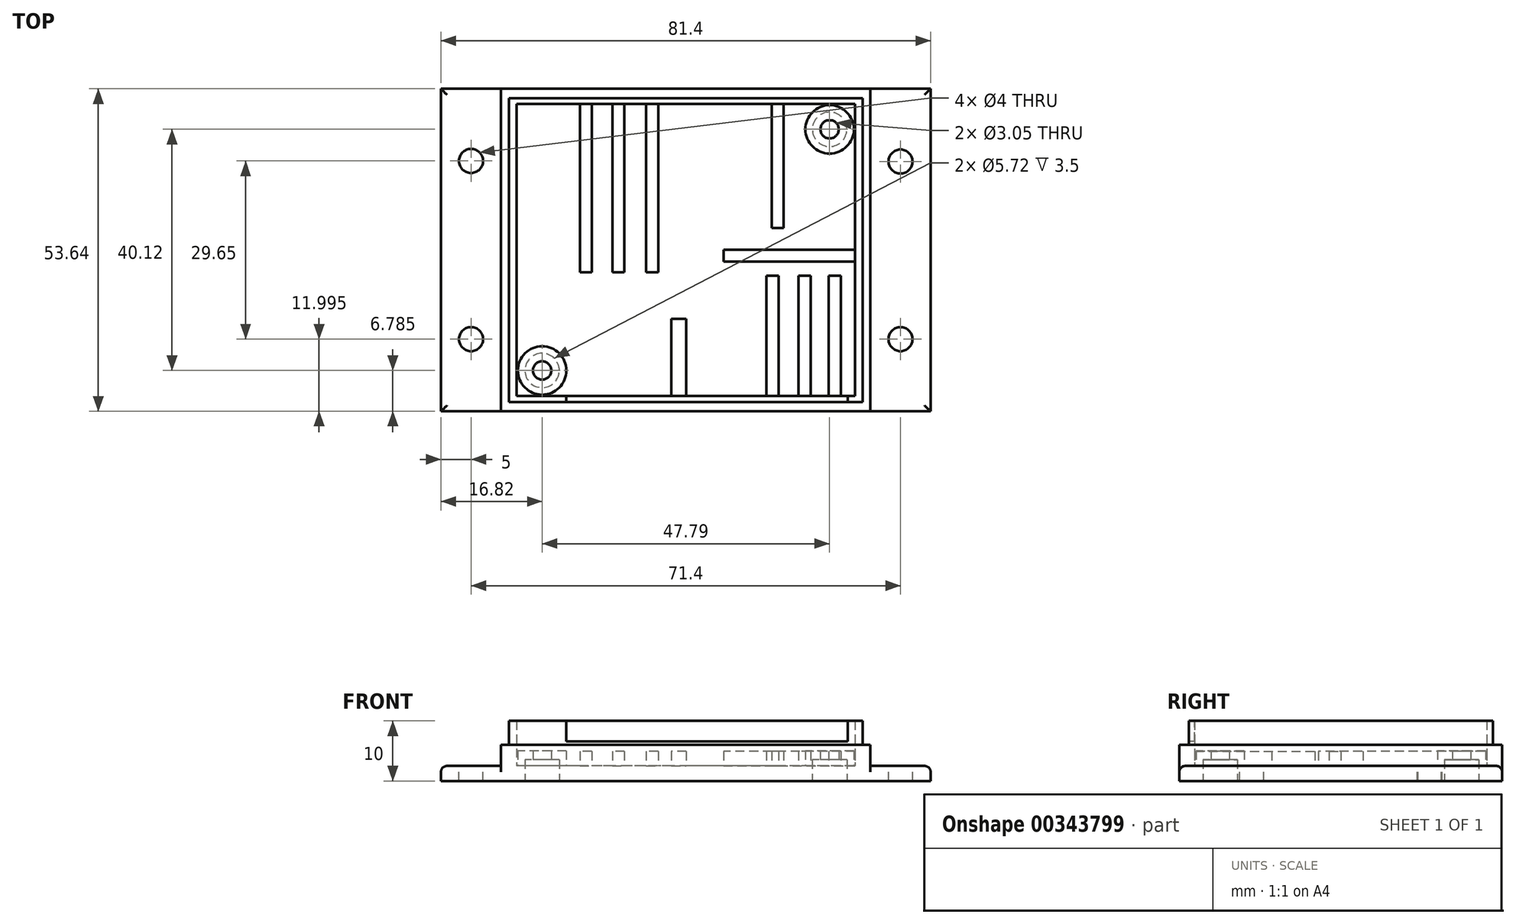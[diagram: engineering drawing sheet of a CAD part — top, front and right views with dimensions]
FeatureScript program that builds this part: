
annotation { "Feature Type Name" : "Feature", "Feature Type Description" : "" }
export const myFeature = defineFeature(function(context is Context, id is Id, definition is map)
    precondition{}
    {
        {
            var Q0;
            Q0=qCreatedBy(makeId("Top.planeOp"),FACE);
            var sketch = newSketch(context, id + "F0", { "sketchPlane" : qUnion([Q0])});
            skLineSegment(sketch, "E0.bottom", {"start": v(26.9, -23.02) * mm, "end": v(-26.9, -23.03) * mm, "construction": true});
            skLineSegment(sketch, "E0.top", {"start": v(26.9, 23.03) * mm, "end": v(-26.9, 23.02) * mm, "construction": true});
            skLineSegment(sketch, "E0.left", {"start": v(26.9, -23.02) * mm, "end": v(26.9, 23.02) * mm, "construction": true});
            skLineSegment(sketch, "E0.right", {"start": v(-26.9, -23.03) * mm, "end": v(-26.9, 23.02) * mm, "construction": true});
            skPoint(sketch, "E0.middle", {"position": v(0, 0) * mm});
            skCircle(sketch, "E1", {"center": v(-23.88, -20.04) * mm, "radius": 1.52 * mm, "construction": true});
            skCircle(sketch, "E2", {"center": v(23.9, 20.09) * mm, "radius": 1.52 * mm, "construction": true});
            skLineSegment(sketch, "E3.0", {"start": v(-28.15, -24.27) * mm, "end": v(-28.15, 24.27) * mm});
            skLineSegment(sketch, "E3.1", {"start": v(28.15, -24.27) * mm, "end": v(-28.15, -24.27) * mm});
            skLineSegment(sketch, "E3.2", {"start": v(28.15, -24.27) * mm, "end": v(28.15, 24.27) * mm});
            skLineSegment(sketch, "E3.3", {"start": v(28.15, 24.27) * mm, "end": v(-28.15, 24.27) * mm});
            skLineSegment(sketch, "E4.0", {"start": v(30.7, 26.82) * mm, "end": v(-30.7, 26.82) * mm});
            skLineSegment(sketch, "E4.1", {"start": v(30.7, -26.82) * mm, "end": v(30.7, 26.82) * mm});
            skLineSegment(sketch, "E4.2", {"start": v(30.7, -26.82) * mm, "end": v(-30.7, -26.82) * mm});
            skLineSegment(sketch, "E4.3", {"start": v(-30.7, -26.82) * mm, "end": v(-30.7, 26.82) * mm});
            skCircle(sketch, "E5", {"center": v(-23.88, -20.04) * mm, "radius": 1.52 * mm});
            skCircle(sketch, "E6", {"center": v(23.9, 20.09) * mm, "radius": 1.52 * mm});
            skCircle(sketch, "E7", {"center": v(-23.88, -20.04) * mm, "radius": 4.03 * mm});
            skCircle(sketch, "E8", {"center": v(23.9, 20.09) * mm, "radius": 4.03 * mm});
            skLineSegment(sketch, "E9.bottom", {"start": v(29.4, -25.27) * mm, "end": v(-29.4, -25.27) * mm});
            skLineSegment(sketch, "E9.top", {"start": v(29.4, 25.27) * mm, "end": v(-29.4, 25.27) * mm});
            skLineSegment(sketch, "E9.left", {"start": v(29.4, -25.27) * mm, "end": v(29.4, 25.27) * mm});
            skLineSegment(sketch, "E9.right", {"start": v(-29.4, -25.27) * mm, "end": v(-29.4, 25.27) * mm});
            skCircle(sketch, "E10", {"center": v(23.9, 20.09) * mm, "radius": 2.86 * mm});
            skCircle(sketch, "E11", {"center": v(-23.88, -20.04) * mm, "radius": 2.86 * mm});
            skLineSegment(sketch, "E12", {"start": v(26.9, -23.02) * mm, "end": v(26.9, -24.27) * mm, "construction": true});
            skCircle(sketch, "E13", {"center": v(-24.03, 20.25) * mm, "radius": 0.65 * mm, "construction": true});
            skCircle(sketch, "E14", {"center": v(-24.03, 1.2) * mm, "radius": 0.65 * mm, "construction": true});
            skCircle(sketch, "E15", {"center": v(8.99, 20.26) * mm, "radius": 0.65 * mm, "construction": true});
            skCircle(sketch, "E16", {"center": v(8.99, 7.56) * mm, "radius": 0.65 * mm, "construction": true});
            skCircle(sketch, "E17", {"center": v(-21, 20.28) * mm, "radius": 0.55 * mm, "construction": true});
            skCircle(sketch, "E18", {"center": v(-21, 12.66) * mm, "radius": 0.55 * mm, "construction": true});
            skCircle(sketch, "E19", {"center": v(-21, 7.58) * mm, "radius": 0.55 * mm, "construction": true});
            skCircle(sketch, "E20", {"center": v(-0.67, 4.12) * mm, "radius": 0.55 * mm, "construction": true});
            skCircle(sketch, "E21", {"center": v(-0.67, 10.12) * mm, "radius": 0.55 * mm, "construction": true});
            skCircle(sketch, "E22", {"center": v(-0.67, 20.28) * mm, "radius": 0.55 * mm, "construction": true});
            skCircle(sketch, "E23", {"center": v(24.2, 15.18) * mm, "radius": 0.5 * mm, "construction": true});
            skCircle(sketch, "E24", {"center": v(24.2, 12.64) * mm, "radius": 0.5 * mm, "construction": true});
            skCircle(sketch, "E25", {"center": v(24.2, 10.1) * mm, "radius": 0.5 * mm, "construction": true});
            skCircle(sketch, "E26", {"center": v(24.2, 7.56) * mm, "radius": 0.5 * mm, "construction": true});
            skCircle(sketch, "E27", {"center": v(24.2, 5.02) * mm, "radius": 0.5 * mm, "construction": true});
            skCircle(sketch, "E28", {"center": v(24.2, 2.48) * mm, "radius": 0.5 * mm, "construction": true});
            skCircle(sketch, "E29", {"center": v(-17.29, -18.54) * mm, "radius": 0.6 * mm, "construction": true});
            skCircle(sketch, "E30", {"center": v(-12.29, -18.54) * mm, "radius": 0.6 * mm, "construction": true});
            skCircle(sketch, "E31", {"center": v(-7.29, -18.54) * mm, "radius": 0.6 * mm, "construction": true});
            skCircle(sketch, "E32", {"center": v(4.95, -18.54) * mm, "radius": 0.6 * mm, "construction": true});
            skCircle(sketch, "E33", {"center": v(9.95, -18.54) * mm, "radius": 0.6 * mm, "construction": true});
            skCircle(sketch, "E34", {"center": v(-23.34, -6.12) * mm, "radius": 0.4 * mm, "construction": true});
            skCircle(sketch, "E35", {"center": v(-23.34, -11.2) * mm, "radius": 0.4 * mm, "construction": true});
            skCircle(sketch, "E36", {"center": v(-18.32, -8.1) * mm, "radius": 0.7 * mm, "construction": true});
            skCircle(sketch, "E37", {"center": v(0.11, -8.1) * mm, "radius": 0.7 * mm, "construction": true});
            skSolve(sketch);
        }
        {
            var Q0;
            Q0=makeQuery(id+"F0.imprint","IMPRINT",FACE,{"disambiguationData":[TD([[makeQuery(id+"F0.imprint","IMPRINT",EDGE,{"derivedFrom":sQuery(id+"F0.wireOp",EDGE,"E3.0")}),-1.0]])]});
            extrude(context, id + "F1", {"entities" : qUnion([Q0]), "depth" : 2.5 * mm});
        }
        {
            var Q0;
            Q0=makeQuery(id+"F0.imprint","IMPRINT",FACE,{"disambiguationData":[TD([[makeQuery(id+"F0.imprint","IMPRINT",EDGE,{"derivedFrom":sQuery(id+"F0.wireOp",EDGE,"E7")}),1.0]])]});
            var Q1;
            Q1=makeQuery(id+"F0.imprint","IMPRINT",FACE,{"disambiguationData":[TD([[makeQuery(id+"F0.imprint","IMPRINT",EDGE,{"derivedFrom":sQuery(id+"F0.wireOp",EDGE,"E5")}),-1.0]])]});
            var Q2;
            Q2=makeQuery(id+"F0.imprint","IMPRINT",FACE,{"disambiguationData":[TD([[makeQuery(id+"F0.imprint","IMPRINT",EDGE,{"derivedFrom":sQuery(id+"F0.wireOp",EDGE,"E8")}),1.0]])]});
            var Q3;
            Q3=makeQuery(id+"F0.imprint","IMPRINT",FACE,{"disambiguationData":[TD([[makeQuery(id+"F0.imprint","IMPRINT",EDGE,{"derivedFrom":sQuery(id+"F0.wireOp",EDGE,"E6")}),-1.0]])]});
            extrude(context, id + "F2", {"entities" : qUnion([Q0, Q1, Q2, Q3]), "operationType" : NewBodyOperationType.ADD, "depth" : 5 * mm});
        }
        {
            var Q0;
            Q0=makeQuery(id+"F0.imprint","IMPRINT",FACE,{"disambiguationData":[TD([[makeQuery(id+"F0.imprint","IMPRINT",EDGE,{"derivedFrom":sQuery(id+"F0.wireOp",EDGE,"E3.0")}),1.0]])]});
            extrude(context, id + "F3", {"entities" : qUnion([Q0]), "operationType" : NewBodyOperationType.ADD, "depth" : 10 * mm});
        }
        {
            var Q0;
            Q0=makeQuery(id+"F0.imprint","IMPRINT",FACE,{"disambiguationData":[TD([[makeQuery(id+"F0.imprint","IMPRINT",EDGE,{"derivedFrom":sQuery(id+"F0.wireOp",EDGE,"E4.0")}),1.0]])]});
            extrude(context, id + "F4", {"entities" : qUnion([Q0]), "operationType" : NewBodyOperationType.ADD, "depth" : 6 * mm});
        }
        {
            var Q0;
            Q0=makeQuery(id+"F0.imprint","IMPRINT",FACE,{"disambiguationData":[TD([[makeQuery(id+"F0.imprint","IMPRINT",EDGE,{"derivedFrom":sQuery(id+"F0.wireOp",EDGE,"E5")}),-1.0]])]});
            var Q1;
            Q1=makeQuery(id+"F0.imprint","IMPRINT",FACE,{"disambiguationData":[TD([[makeQuery(id+"F0.imprint","IMPRINT",EDGE,{"derivedFrom":sQuery(id+"F0.wireOp",EDGE,"E6")}),-1.0]])]});
            extrude(context, id + "F5", {"entities" : qUnion([Q0, Q1]), "operationType" : NewBodyOperationType.REMOVE, "depth" : 3.5 * mm});
        }
        {
            var Q0;
            Q0=makeQuery(id+"F4.opExtrude","SWEPT_FACE",FACE,{"disambiguationData":[OSD([sQuery(id+"F0.wireOp",EDGE,"E4.3")])]});
            var sketch = newSketch(context, id + "F6", { "sketchPlane" : qUnion([Q0])});
            skLineSegment(sketch, "E38", {"start": v(-26.82, 2.5) * mm, "end": v(26.82, 2.5) * mm});
            skSolve(sketch);
        }
        {
            var Q0;
            Q0=makeQuery(id+"F4.opExtrude","SWEPT_FACE",FACE,{"disambiguationData":[OSD([sQuery(id+"F0.wireOp",EDGE,"E4.1")])]});
            var sketch = newSketch(context, id + "F7", { "sketchPlane" : qUnion([Q0])});
            skLineSegment(sketch, "E39", {"start": v(-26.82, 2.5) * mm, "end": v(26.82, 2.5) * mm});
            skSolve(sketch);
        }
        {
            var Q0;
            {var subQ0=sQuery(id+"F6.wireOp",EDGE,"E38");Q0=makeQuery(id+"F6.imprint","IMPRINT",FACE,{"disambiguationData":[TD([[makeQuery(id+"F6.imprint","IMPRINT",EDGE,{"derivedFrom":subQ0}),-1.0]])]});}
            extrude(context, id + "F8", {"entities" : qUnion([Q0]), "operationType" : NewBodyOperationType.ADD, "depth" : 10 * mm});
        }
        {
            var Q0;
            {var subQ0=sQuery(id+"F7.wireOp",EDGE,"E39");Q0=makeQuery(id+"F7.imprint","IMPRINT",FACE,{"disambiguationData":[TD([[makeQuery(id+"F7.imprint","IMPRINT",EDGE,{"derivedFrom":subQ0}),-1.0]])]});}
            extrude(context, id + "F9", {"entities" : qUnion([Q0]), "operationType" : NewBodyOperationType.ADD, "depth" : 10 * mm});
        }
        {
            var Q0;
            Q0=makeQuery(id+"F8.opExtrude","SWEPT_FACE",FACE,{"disambiguationData":[OSD([sQuery(id+"F6.wireOp",EDGE,"E38")])]});
            var sketch = newSketch(context, id + "F10", { "sketchPlane" : qUnion([Q0])});
            skCircle(sketch, "E40", {"center": v(-35.7, 14.82) * mm, "radius": 2 * mm});
            skCircle(sketch, "E41", {"center": v(-35.7, -14.82) * mm, "radius": 2 * mm});
            skSolve(sketch);
        }
        {
            var Q0;
            Q0=makeQuery(id+"F9.opExtrude","SWEPT_FACE",FACE,{"disambiguationData":[OSD([sQuery(id+"F7.wireOp",EDGE,"E39")])]});
            var sketch = newSketch(context, id + "F11", { "sketchPlane" : qUnion([Q0])});
            skCircle(sketch, "E42", {"center": v(35.7, -14.82) * mm, "radius": 2 * mm});
            skCircle(sketch, "E43", {"center": v(35.7, 14.73) * mm, "radius": 2 * mm});
            skSolve(sketch);
        }
        {
            var Q0;
            Q0=makeQuery(id+"F10.imprint","IMPRINT",FACE,{"disambiguationData":[TD([[makeQuery(id+"F10.imprint","IMPRINT",EDGE,{"derivedFrom":sQuery(id+"F10.wireOp",EDGE,"E40")}),1.0]])]});
            var Q1;
            Q1=makeQuery(id+"F10.imprint","IMPRINT",FACE,{"disambiguationData":[TD([[makeQuery(id+"F10.imprint","IMPRINT",EDGE,{"derivedFrom":sQuery(id+"F10.wireOp",EDGE,"E41")}),1.0]])]});
            var Q2;
            Q2=makeQuery(id+"F11.imprint","IMPRINT",FACE,{"disambiguationData":[TD([[makeQuery(id+"F11.imprint","IMPRINT",EDGE,{"derivedFrom":sQuery(id+"F11.wireOp",EDGE,"E43")}),1.0]])]});
            var Q3;
            Q3=makeQuery(id+"F11.imprint","IMPRINT",FACE,{"disambiguationData":[TD([[makeQuery(id+"F11.imprint","IMPRINT",EDGE,{"derivedFrom":sQuery(id+"F11.wireOp",EDGE,"E42")}),1.0]])]});
            extrude(context, id + "F12", {"entities" : qUnion([Q0, Q1, Q2, Q3]), "operationType" : NewBodyOperationType.REMOVE, "oppositeDirection" : true, "depth" : 2.5 * mm});
        }
        {
            var Q0;
            Q0=makeQuery(id+"F3.opExtrude","CAP_FACE",FACE,{"disambiguationData":[OSD([sQuery(id+"F0.wireOp",EDGE,"E3.0"),sQuery(id+"F0.wireOp",EDGE,"E3.1"),sQuery(id+"F0.wireOp",EDGE,"E3.2"),sQuery(id+"F0.wireOp",EDGE,"E3.3"),sQuery(id+"F0.wireOp",EDGE,"E9.bottom"),sQuery(id+"F0.wireOp",EDGE,"E9.top"),sQuery(id+"F0.wireOp",EDGE,"E9.left"),sQuery(id+"F0.wireOp",EDGE,"E9.right")])],"isStart":false});
            var sketch = newSketch(context, id + "F13", { "sketchPlane" : qUnion([Q0])});
            skLineSegment(sketch, "E44", {"start": v(26.9, -24.27) * mm, "end": v(26.9, -26.77) * mm});
            skLineSegment(sketch, "E45", {"start": v(26.9, -26.77) * mm, "end": v(-19.85, -26.77) * mm});
            skLineSegment(sketch, "E46", {"start": v(-19.85, -26.77) * mm, "end": v(-19.85, -24.27) * mm});
            skSolve(sketch);
        }
        {
            var Q0;
            {var subQ0=sQuery(id+"F13.wireOp",EDGE,"E44");var subQ1=makeQuery(id+"F3.opExtrude","CAP_EDGE",EDGE,{"disambiguationData":[OSD([sQuery(id+"F0.wireOp",EDGE,"E3.1")])],"isStart":false});var subQ2=makeQuery(id+"F13.imprint","INTERSECT",VERTEX,{"derivedFrom":[subQ1,subQ0]});Q0=makeQuery(id+"F13.imprint","IMPRINT",FACE,{"disambiguationData":[TD([[makeQuery(id+"F13.imprint","IMPRINT",EDGE,{"disambiguationData":[TD([[subQ2,-1.0]])],"derivedFrom":subQ0}),-1.0]])]});}
            var Q1;
            {var subQ0=sQuery(id+"F13.wireOp",EDGE,"E45");Q1=makeQuery(id+"F13.imprint","IMPRINT",FACE,{"disambiguationData":[TD([[makeQuery(id+"F13.imprint","IMPRINT",EDGE,{"derivedFrom":subQ0}),-1.0]])]});}
            extrude(context, id + "F14", {"entities" : qUnion([Q0, Q1]), "operationType" : NewBodyOperationType.REMOVE, "oppositeDirection" : true, "depth" : 3.4 * mm});
        }
        {
            var Q0;
            Q0=makeQuery(id+"F1.opExtrude","CAP_FACE",FACE,{"disambiguationData":[OSD([sQuery(id+"F0.wireOp",EDGE,"E3.0"),sQuery(id+"F0.wireOp",EDGE,"E3.1"),sQuery(id+"F0.wireOp",EDGE,"E3.2"),sQuery(id+"F0.wireOp",EDGE,"E3.3"),sQuery(id+"F0.wireOp",EDGE,"E7"),sQuery(id+"F0.wireOp",EDGE,"E8")])],"isStart":false});
            var sketch = newSketch(context, id + "F15", { "sketchPlane" : qUnion([Q0])});
            skLineSegment(sketch, "E47", {"start": v(-12.2, 24.27) * mm, "end": v(-12.2, -3.73) * mm});
            skLineSegment(sketch, "E48", {"start": v(-12.2, -3.73) * mm, "end": v(-10.2, -3.73) * mm});
            skLineSegment(sketch, "E49", {"start": v(-10.2, -3.73) * mm, "end": v(-10.2, 24.27) * mm});
            skLineSegment(sketch, "E50", {"start": v(-6.58, 24.27) * mm, "end": v(-6.58, -3.73) * mm});
            skLineSegment(sketch, "E51", {"start": v(-6.58, -3.73) * mm, "end": v(-4.58, -3.73) * mm});
            skLineSegment(sketch, "E52", {"start": v(-4.58, -3.73) * mm, "end": v(-4.58, 24.27) * mm});
            skLineSegment(sketch, "E53", {"start": v(28.15, 0.05) * mm, "end": v(6.27, 0.05) * mm});
            skLineSegment(sketch, "E54", {"start": v(6.27, 0.05) * mm, "end": v(6.27, -1.95) * mm});
            skLineSegment(sketch, "E55", {"start": v(6.27, -1.95) * mm, "end": v(28.15, -1.95) * mm});
            skLineSegment(sketch, "E56", {"start": v(14.26, 24.27) * mm, "end": v(14.26, 3.7) * mm});
            skLineSegment(sketch, "E57", {"start": v(14.26, 3.7) * mm, "end": v(16.26, 3.7) * mm});
            skLineSegment(sketch, "E58", {"start": v(16.26, 3.7) * mm, "end": v(16.26, 24.27) * mm});
            skLineSegment(sketch, "E59", {"start": v(25.77, -24.27) * mm, "end": v(25.77, -4.27) * mm});
            skLineSegment(sketch, "E60", {"start": v(25.77, -4.27) * mm, "end": v(23.77, -4.27) * mm});
            skLineSegment(sketch, "E61", {"start": v(23.77, -4.27) * mm, "end": v(23.77, -24.27) * mm});
            skLineSegment(sketch, "E62", {"start": v(20.76, -24.27) * mm, "end": v(20.76, -4.27) * mm});
            skLineSegment(sketch, "E63", {"start": v(20.76, -4.27) * mm, "end": v(18.76, -4.27) * mm});
            skLineSegment(sketch, "E64", {"start": v(18.76, -4.27) * mm, "end": v(18.76, -24.27) * mm});
            skLineSegment(sketch, "E65", {"start": v(15.42, -24.27) * mm, "end": v(15.42, -4.27) * mm});
            skLineSegment(sketch, "E66", {"start": v(15.42, -4.27) * mm, "end": v(13.42, -4.27) * mm});
            skLineSegment(sketch, "E67", {"start": v(13.42, -4.27) * mm, "end": v(13.42, -24.27) * mm});
            skLineSegment(sketch, "E68", {"start": v(-17.62, 24.27) * mm, "end": v(-17.62, -3.73) * mm});
            skLineSegment(sketch, "E69", {"start": v(-17.62, -3.73) * mm, "end": v(-15.62, -3.73) * mm});
            skLineSegment(sketch, "E70", {"start": v(-15.62, -3.73) * mm, "end": v(-15.62, 24.27) * mm});
            skLineSegment(sketch, "E71", {"start": v(-2.41, -24.27) * mm, "end": v(-2.41, -11.44) * mm});
            skLineSegment(sketch, "E72", {"start": v(-2.41, -11.44) * mm, "end": v(0.09, -11.44) * mm});
            skLineSegment(sketch, "E73", {"start": v(0.09, -11.44) * mm, "end": v(0.09, -24.27) * mm});
            skSolve(sketch);
        }
        {
            var Q0;
            {var subQ0=sQuery(id+"F15.wireOp",EDGE,"E68");Q0=makeQuery(id+"F15.imprint","IMPRINT",FACE,{"disambiguationData":[TD([[makeQuery(id+"F15.imprint","IMPRINT",EDGE,{"derivedFrom":subQ0}),1.0]])]});}
            var Q1;
            {var subQ0=sQuery(id+"F15.wireOp",EDGE,"E47");Q1=makeQuery(id+"F15.imprint","IMPRINT",FACE,{"disambiguationData":[TD([[makeQuery(id+"F15.imprint","IMPRINT",EDGE,{"derivedFrom":subQ0}),1.0]])]});}
            var Q2;
            {var subQ0=sQuery(id+"F15.wireOp",EDGE,"E50");Q2=makeQuery(id+"F15.imprint","IMPRINT",FACE,{"disambiguationData":[TD([[makeQuery(id+"F15.imprint","IMPRINT",EDGE,{"derivedFrom":subQ0}),1.0]])]});}
            var Q3;
            {var subQ0=sQuery(id+"F15.wireOp",EDGE,"E56");Q3=makeQuery(id+"F15.imprint","IMPRINT",FACE,{"disambiguationData":[TD([[makeQuery(id+"F15.imprint","IMPRINT",EDGE,{"derivedFrom":subQ0}),1.0]])]});}
            var Q4;
            {var subQ0=sQuery(id+"F15.wireOp",EDGE,"E53");Q4=makeQuery(id+"F15.imprint","IMPRINT",FACE,{"disambiguationData":[TD([[makeQuery(id+"F15.imprint","IMPRINT",EDGE,{"derivedFrom":subQ0}),1.0]])]});}
            var Q5;
            {var subQ0=sQuery(id+"F15.wireOp",EDGE,"E65");Q5=makeQuery(id+"F15.imprint","IMPRINT",FACE,{"disambiguationData":[TD([[makeQuery(id+"F15.imprint","IMPRINT",EDGE,{"derivedFrom":subQ0}),1.0]])]});}
            var Q6;
            {var subQ0=sQuery(id+"F15.wireOp",EDGE,"E62");Q6=makeQuery(id+"F15.imprint","IMPRINT",FACE,{"disambiguationData":[TD([[makeQuery(id+"F15.imprint","IMPRINT",EDGE,{"derivedFrom":subQ0}),1.0]])]});}
            var Q7;
            {var subQ0=sQuery(id+"F15.wireOp",EDGE,"E59");Q7=makeQuery(id+"F15.imprint","IMPRINT",FACE,{"disambiguationData":[TD([[makeQuery(id+"F15.imprint","IMPRINT",EDGE,{"derivedFrom":subQ0}),1.0]])]});}
            var Q8;
            {var subQ0=sQuery(id+"F15.wireOp",EDGE,"E71");Q8=makeQuery(id+"F15.imprint","IMPRINT",FACE,{"disambiguationData":[TD([[makeQuery(id+"F15.imprint","IMPRINT",EDGE,{"derivedFrom":subQ0}),-1.0]])]});}
            extrude(context, id + "F16", {"entities" : qUnion([Q0, Q1, Q2, Q3, Q4, Q5, Q6, Q7, Q8]), "operationType" : NewBodyOperationType.ADD, "depth" : 2.4 * mm});
        }
        {
            var Q0;
            Q0=makeQuery(id+"F8.opExtrude","CAP_EDGE",EDGE,{"disambiguationData":[OSD([sQuery(id+"F6.wireOp",EDGE,"E38")])],"isStart":false});
            var Q1;
            Q1=makeQuery(id+"F9.opExtrude","CAP_EDGE",EDGE,{"disambiguationData":[OSD([sQuery(id+"F7.wireOp",EDGE,"E39")])],"isStart":false});
            var Q2;
            Q2=makeQuery(id+"F8.opExtrude","SWEPT_EDGE",EDGE,{"disambiguationData":[OSD([sQuery(id+"F0.wireOp",EDGE,"E4.0"),sQuery(id+"F0.wireOp",EDGE,"E4.3"),sQuery(id+"F6.wireOp",EDGE,"E38")])]});
            var Q3;
            Q3=makeQuery(id+"F8.opExtrude","SWEPT_EDGE",EDGE,{"disambiguationData":[OSD([sQuery(id+"F0.wireOp",EDGE,"E4.2"),sQuery(id+"F0.wireOp",EDGE,"E4.3"),sQuery(id+"F6.wireOp",EDGE,"E38")])]});
            var Q4;
            Q4=makeQuery(id+"F9.opExtrude","SWEPT_EDGE",EDGE,{"disambiguationData":[OSD([sQuery(id+"F0.wireOp",EDGE,"E4.1"),sQuery(id+"F0.wireOp",EDGE,"E4.2"),sQuery(id+"F7.wireOp",EDGE,"E39")])]});
            var Q5;
            Q5=makeQuery(id+"F9.opExtrude","SWEPT_EDGE",EDGE,{"disambiguationData":[OSD([sQuery(id+"F0.wireOp",EDGE,"E4.0"),sQuery(id+"F0.wireOp",EDGE,"E4.1"),sQuery(id+"F7.wireOp",EDGE,"E39")])]});
            fillet(context, id + "F17", {"entities" : qUnion([Q0, Q1, Q2, Q3, Q4, Q5]), "radius" : 1 * mm, "tangentPropagation" : true, "allowEdgeOverflow" : false});
        }
    });
